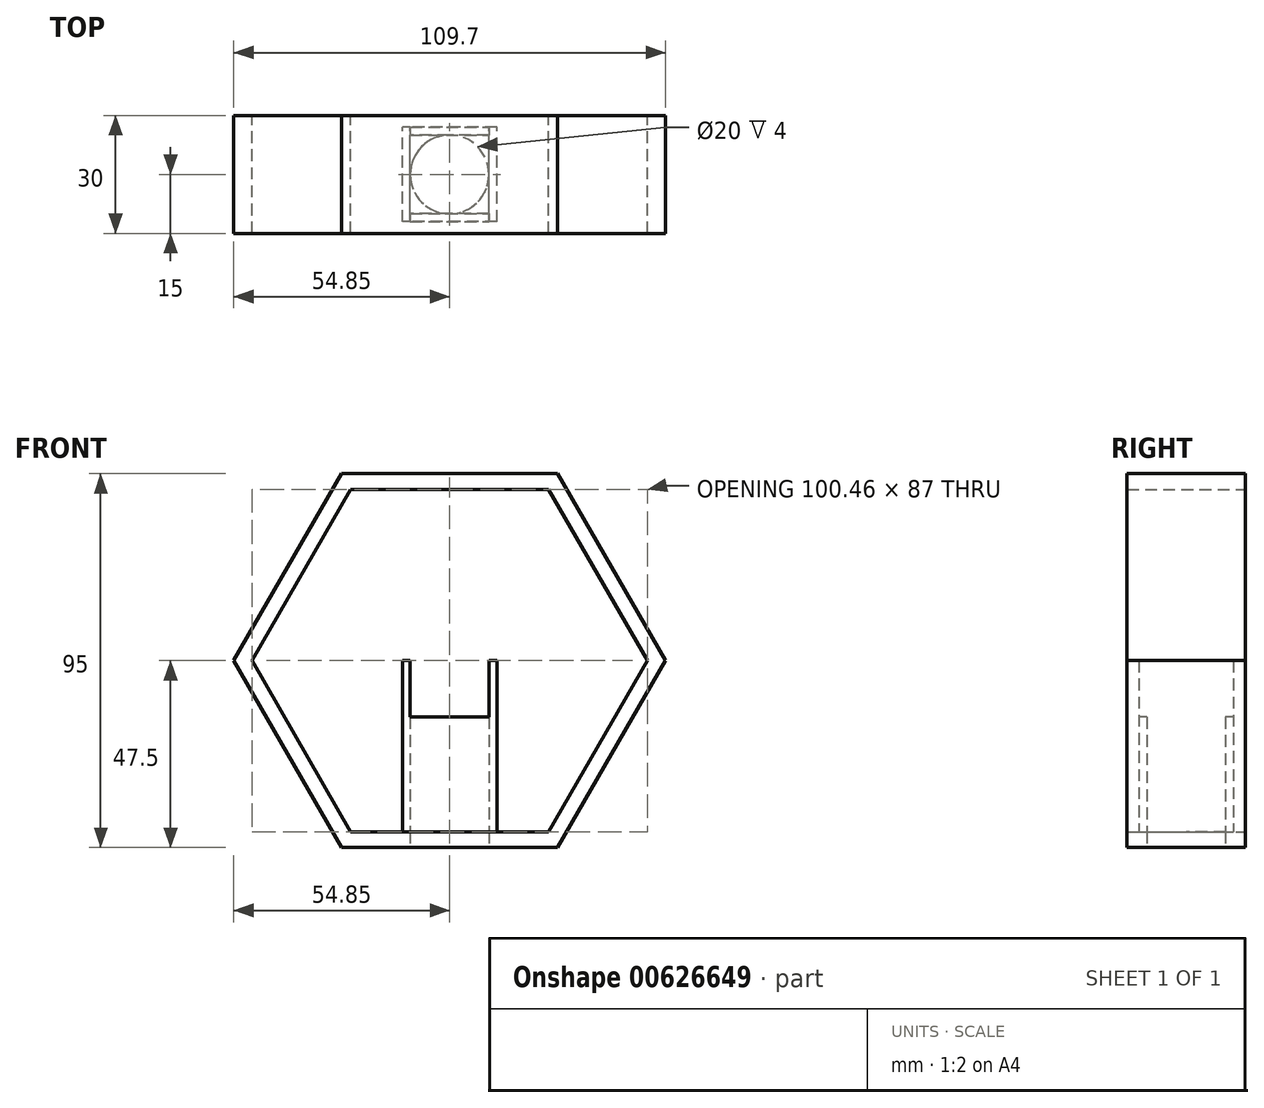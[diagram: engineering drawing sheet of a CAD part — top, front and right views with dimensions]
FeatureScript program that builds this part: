
annotation { "Feature Type Name" : "Feature", "Feature Type Description" : "" }
export const myFeature = defineFeature(function(context is Context, id is Id, definition is map)
    precondition{}
    {
        {
            var Q0;
            Q0=qCreatedBy(makeId("Front.planeOp"),FACE);
            var sketch = newSketch(context, id + "F0", { "sketchPlane" : qUnion([Q0])});
            skCircle(sketch, "E0.cCircle", {"center": v(0, 0) * mm, "radius": 47.5 * mm, "construction": true});
            skLineSegment(sketch, "E0.0", {"start": v(27.42, -47.5) * mm, "end": v(-27.42, -47.5) * mm});
            skLineSegment(sketch, "E0.1", {"start": v(-27.42, -47.5) * mm, "end": v(-54.85, 0) * mm});
            skLineSegment(sketch, "E0.2", {"start": v(-54.85, 0) * mm, "end": v(-27.42, 47.5) * mm});
            skLineSegment(sketch, "E0.3", {"start": v(-27.42, 47.5) * mm, "end": v(27.42, 47.5) * mm});
            skLineSegment(sketch, "E0.4", {"start": v(27.42, 47.5) * mm, "end": v(54.85, 0) * mm});
            skLineSegment(sketch, "E0.5", {"start": v(54.85, 0) * mm, "end": v(27.42, -47.5) * mm});
            skPoint(sketch, "E0.0.midPoint", {"position": v(0, -47.5) * mm});
            skCircle(sketch, "E1.cCircle", {"center": v(0, 0) * mm, "radius": 43.5 * mm, "construction": true});
            skLineSegment(sketch, "E1.0", {"start": v(25.11, -43.5) * mm, "end": v(-25.11, -43.5) * mm});
            skLineSegment(sketch, "E1.1", {"start": v(-25.11, -43.5) * mm, "end": v(-50.23, 0) * mm});
            skLineSegment(sketch, "E1.2", {"start": v(-50.23, 0) * mm, "end": v(-25.11, 43.5) * mm});
            skLineSegment(sketch, "E1.3", {"start": v(-25.11, 43.5) * mm, "end": v(25.11, 43.5) * mm});
            skLineSegment(sketch, "E1.4", {"start": v(25.11, 43.5) * mm, "end": v(50.23, 0) * mm});
            skLineSegment(sketch, "E1.5", {"start": v(50.23, 0) * mm, "end": v(25.11, -43.5) * mm});
            skPoint(sketch, "E1.0.midPoint", {"position": v(0, -43.5) * mm});
            skSolve(sketch);
        }
        {
            var Q0;
            Q0=makeQuery(id+"F0.imprint","IMPRINT",FACE,{"disambiguationData":[TD([[makeQuery(id+"F0.imprint","IMPRINT",EDGE,{"derivedFrom":sQuery(id+"F0.wireOp",EDGE,"E0.0")}),-1.0]])]});
            extrude(context, id + "F1", {"entities" : qUnion([Q0]), "depth" : 30 * mm, "offsetDistance" : 25 * mm});
        }
        {
            var Q0;
            Q0=makeQuery(id+"F1.opExtrude","SWEPT_FACE",FACE,{"disambiguationData":[OSD([sQuery(id+"F0.wireOp",EDGE,"E0.0")])]});
            var sketch = newSketch(context, id + "F2", { "sketchPlane" : qUnion([Q0])});
            skCircle(sketch, "E2", {"center": v(0, 15) * mm, "radius": 10 * mm});
            skSolve(sketch);
        }
        {
            var Q0;
            Q0 = qSketchRegion(id + "F2", true);
            var Q1;
            Q1=makeQuery(id+"F1.opExtrude","SWEPT_FACE",FACE,{"disambiguationData":[OSD([sQuery(id+"F0.wireOp",EDGE,"E1.0")])]});
            extrude(context, id + "F3", {"entities" : qUnion([Q0]), "operationType" : NewBodyOperationType.REMOVE, "endBound" : BoundingType.UP_TO_SURFACE, "oppositeDirection" : true, "depth" : 25 * mm, "endBoundEntityFace" : qUnion([Q1]), "offsetDistance" : 25 * mm});
        }
        {
            var Q0;
            Q0=makeQuery(id+"F1.opExtrude","SWEPT_FACE",FACE,{"disambiguationData":[OSD([sQuery(id+"F0.wireOp",EDGE,"E1.0")])]});
            var sketch = newSketch(context, id + "F4", { "sketchPlane" : qUnion([Q0])});
            skLineSegment(sketch, "E3.bottom", {"start": v(12, -27) * mm, "end": v(-12, -27) * mm});
            skLineSegment(sketch, "E3.top", {"start": v(12, -3) * mm, "end": v(-12, -3) * mm});
            skLineSegment(sketch, "E3.left", {"start": v(12, -27) * mm, "end": v(12, -3) * mm});
            skLineSegment(sketch, "E3.right", {"start": v(-12, -27) * mm, "end": v(-12, -3) * mm});
            skPoint(sketch, "E3.middle", {"position": v(0, -15) * mm});
            skLineSegment(sketch, "E4.bottom", {"start": v(10, -25) * mm, "end": v(-10, -25) * mm});
            skLineSegment(sketch, "E4.top", {"start": v(10, -5) * mm, "end": v(-10, -5) * mm});
            skLineSegment(sketch, "E4.left", {"start": v(10, -25) * mm, "end": v(10, -5) * mm});
            skLineSegment(sketch, "E4.right", {"start": v(-10, -25) * mm, "end": v(-10, -5) * mm});
            skSolve(sketch);
        }
        {
            var Q0;
            Q0=makeQuery(id+"F4.imprint","IMPRINT",FACE,{"disambiguationData":[TD([[makeQuery(id+"F4.imprint","IMPRINT",EDGE,{"derivedFrom":sQuery(id+"F4.wireOp",EDGE,"E3.bottom")}),-1.0]])]});
            extrude(context, id + "F5", {"entities" : qUnion([Q0]), "operationType" : NewBodyOperationType.ADD, "depth" : 43.5 * mm, "offsetDistance" : 25 * mm});
        }
        {
            var Q0;
            Q0=makeQuery(id+"F5.opExtrude","SWEPT_FACE",FACE,{"disambiguationData":[OSD([sQuery(id+"F4.wireOp",EDGE,"E3.bottom")])]});
            var sketch = newSketch(context, id + "F6", { "sketchPlane" : qUnion([Q0])});
            skLineSegment(sketch, "E5.bottom", {"start": v(-10, 0) * mm, "end": v(10, 0) * mm});
            skLineSegment(sketch, "E5.top", {"start": v(-10, -14.35) * mm, "end": v(10, -14.35) * mm});
            skLineSegment(sketch, "E5.left", {"start": v(-10, 0) * mm, "end": v(-10, -14.35) * mm});
            skLineSegment(sketch, "E5.right", {"start": v(10, 0) * mm, "end": v(10, -14.35) * mm});
            skSolve(sketch);
        }
        {
            var Q0;
            Q0=makeQuery(id+"F6.imprint","IMPRINT",FACE,{"disambiguationData":[TD([[makeQuery(id+"F6.imprint","IMPRINT",EDGE,{"derivedFrom":sQuery(id+"F6.wireOp",EDGE,"E5.bottom")}),1.0]])]});
            extrude(context, id + "F7", {"entities" : qUnion([Q0]), "operationType" : NewBodyOperationType.REMOVE, "oppositeDirection" : true, "depth" : 28.1 * mm, "offsetDistance" : 25 * mm});
        }
    });
